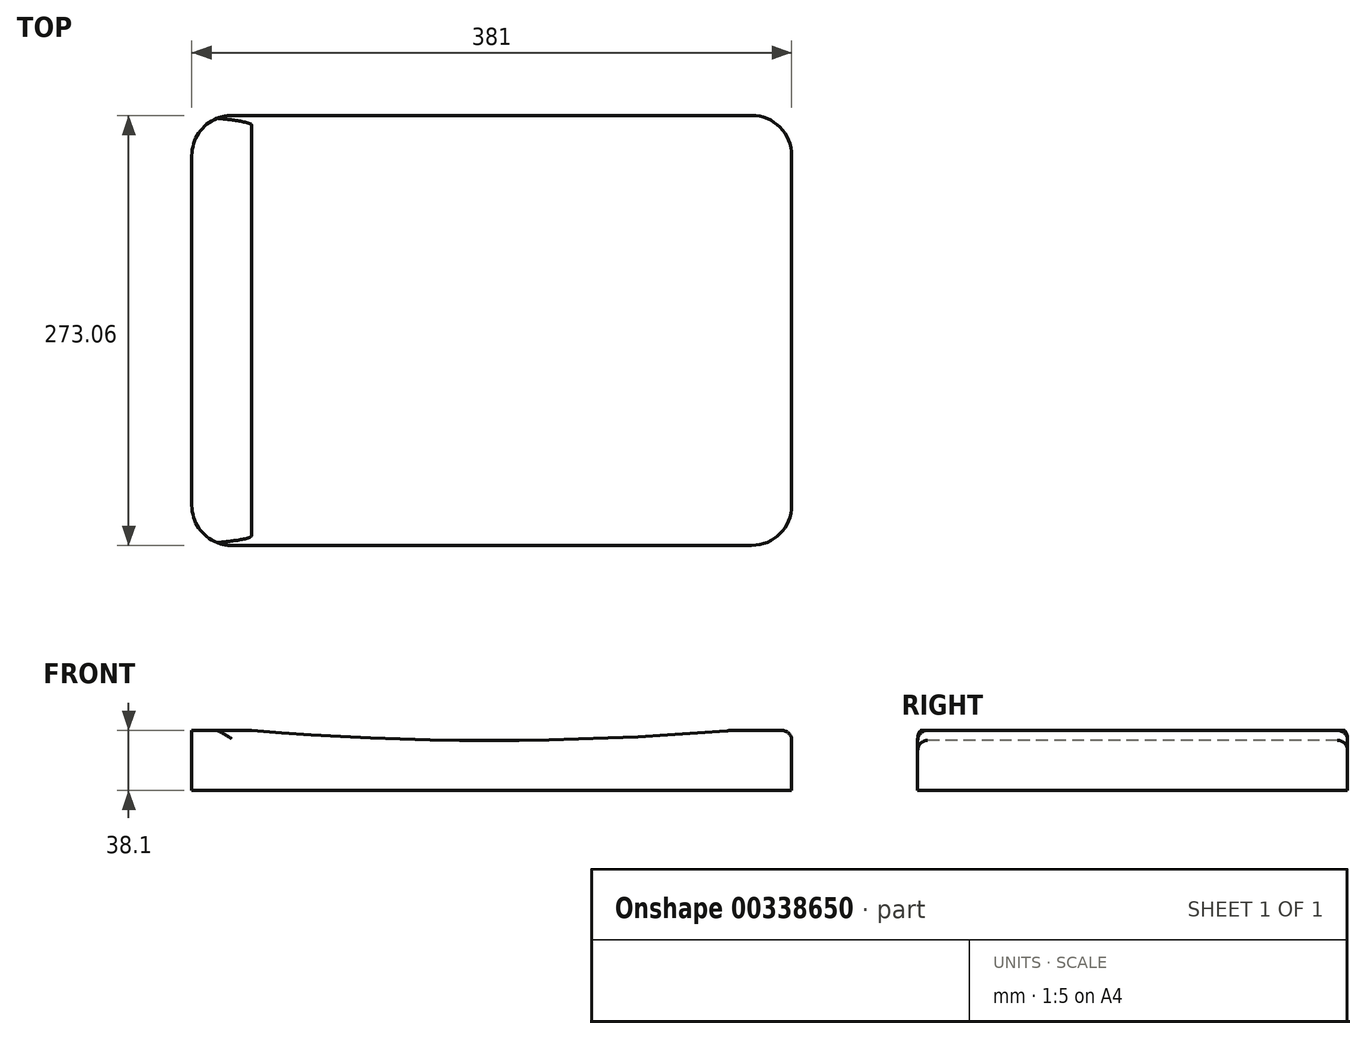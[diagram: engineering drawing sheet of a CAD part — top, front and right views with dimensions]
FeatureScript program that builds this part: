
annotation { "Feature Type Name" : "Feature", "Feature Type Description" : "" }
export const myFeature = defineFeature(function(context is Context, id is Id, definition is map)
    precondition{}
    {
        {
            var Q0;
            Q0=qCreatedBy(makeId("Top.planeOp"),FACE);
            var sketch = newSketch(context, id + "F0", { "sketchPlane" : qUnion([Q0])});
            skLineSegment(sketch, "E0.bottom", {"start": v(190.5, 136.53) * mm, "end": v(-190.5, 136.53) * mm});
            skLineSegment(sketch, "E0.top", {"start": v(190.5, -136.53) * mm, "end": v(-190.5, -136.53) * mm});
            skLineSegment(sketch, "E0.left", {"start": v(190.5, 136.53) * mm, "end": v(190.5, -136.53) * mm});
            skLineSegment(sketch, "E0.right", {"start": v(-190.5, 136.53) * mm, "end": v(-190.5, -136.53) * mm});
            skPoint(sketch, "E0.middle", {"position": v(0, 0) * mm});
            skSolve(sketch);
        }
        {
            var Q0;
            Q0 = qSketchRegion(id + "F0", true);
            extrude(context, id + "F1", {"entities" : qUnion([Q0]), "depth" : 38.1 * mm});
        }
        {
            var Q0;
            Q0=makeQuery(id+"F1.opExtrude","SWEPT_FACE",FACE,{"disambiguationData":[OSD([sQuery(id+"F0.wireOp",EDGE,"E0.top")])]});
            var sketch = newSketch(context, id + "F2", { "sketchPlane" : qUnion([Q0])});
            skArc(sketch, "E1", {"start": v(-152.4, 38.1) * mm, "mid": v(0, 31.75) * mm, "end": v(152.4, 38.1) * mm});
            skLineSegment(sketch, "E2", {"start": v(-152.4, 38.1) * mm, "end": v(152.4, 38.1) * mm});
            skLineSegment(sketch, "E3", {"start": v(0, 0) * mm, "end": v(0, 31.75) * mm, "construction": true});
            skSolve(sketch);
        }
        {
            var Q0;
            Q0 = qSketchRegion(id + "F2", true);
            extrude(context, id + "F3", {"entities" : qUnion([Q0]), "operationType" : NewBodyOperationType.REMOVE, "endBound" : BoundingType.THROUGH_ALL, "oppositeDirection" : true, "depth" : 25.4 * mm});
        }
        {
            var Q0;
            {var subQ0=sQuery(id+"F2.wireOp",EDGE,"E2");var subQ1=sQuery(id+"F2.wireOp",EDGE,"E1");var subQ2=sQuery(id+"F0.wireOp",EDGE,"E0.top");Q0=makeQuery(id+"F3.boolean.opBoolean","COPY",EDGE,{"derivedFrom":makeQuery(id+"F3.opExtrude","SWEPT_EDGE",EDGE,{"disambiguationData":[OSD([subQ2,subQ1,subQ0]),TDD([makeQuery(id+"F2.imprint","INTERSECT",VERTEX,{"disambiguationData":[OD(0.0)],"derivedFrom":[makeQuery(id+"F1.opExtrude","CAP_EDGE",EDGE,{"disambiguationData":[OSD([subQ2])],"isStart":false}),subQ1,subQ0]})])]})});}
            var Q1;
            {var subQ0=sQuery(id+"F2.wireOp",EDGE,"E2");var subQ1=sQuery(id+"F2.wireOp",EDGE,"E1");var subQ2=sQuery(id+"F0.wireOp",EDGE,"E0.top");Q1=makeQuery(id+"F3.boolean.opBoolean","COPY",EDGE,{"derivedFrom":makeQuery(id+"F3.opExtrude","SWEPT_EDGE",EDGE,{"disambiguationData":[OSD([subQ2,subQ1,subQ0]),TDD([makeQuery(id+"F2.imprint","INTERSECT",VERTEX,{"disambiguationData":[OD(1.0)],"derivedFrom":[makeQuery(id+"F1.opExtrude","CAP_EDGE",EDGE,{"disambiguationData":[OSD([subQ2])],"isStart":false}),subQ1,subQ0]})])]})});}
            fillet(context, id + "F4", {"entities" : qUnion([Q0, Q1]), "radius" : 76.2 * mm, "tangentPropagation" : true, "allowEdgeOverflow" : false});
        }
        {
            var Q0;
            Q0=makeQuery(id+"F1.opExtrude","SWEPT_EDGE",EDGE,{"disambiguationData":[OSD([sQuery(id+"F0.wireOp",EDGE,"E0.top"),sQuery(id+"F0.wireOp",EDGE,"E0.right")])]});
            var Q1;
            Q1=makeQuery(id+"F1.opExtrude","SWEPT_EDGE",EDGE,{"disambiguationData":[OSD([sQuery(id+"F0.wireOp",EDGE,"E0.top"),sQuery(id+"F0.wireOp",EDGE,"E0.left")])]});
            var Q2;
            Q2=makeQuery(id+"F1.opExtrude","SWEPT_EDGE",EDGE,{"disambiguationData":[OSD([sQuery(id+"F0.wireOp",EDGE,"E0.bottom"),sQuery(id+"F0.wireOp",EDGE,"E0.left")])]});
            var Q3;
            Q3=makeQuery(id+"F1.opExtrude","SWEPT_EDGE",EDGE,{"disambiguationData":[OSD([sQuery(id+"F0.wireOp",EDGE,"E0.bottom"),sQuery(id+"F0.wireOp",EDGE,"E0.right")])]});
            fillet(context, id + "F5", {"entities" : qUnion([Q0, Q1, Q2, Q3]), "radius" : 25.4 * mm, "tangentPropagation" : true, "allowEdgeOverflow" : false});
        }
        {
            var Q0;
            {var subQ0=sQuery(id+"F0.wireOp",EDGE,"E0.bottom");var subQ1=sQuery(id+"F0.wireOp",EDGE,"E0.left");Q0=makeQuery(id+"F3.boolean.opBoolean","SPLIT",EDGE,{"disambiguationData":[TD([makeQuery(id+"F1.opExtrude","SWEPT_FACE",FACE,{"disambiguationData":[OSD([subQ1])]})])],"derivedFrom":makeQuery(id+"F1.opExtrude","CAP_EDGE",EDGE,{"disambiguationData":[OSD([subQ0])],"isStart":false})});}
            fillet(context, id + "F6", {"entities" : qUnion([Q0]), "radius" : 6.35 * mm, "tangentPropagation" : true, "allowEdgeOverflow" : false});
        }
    });
